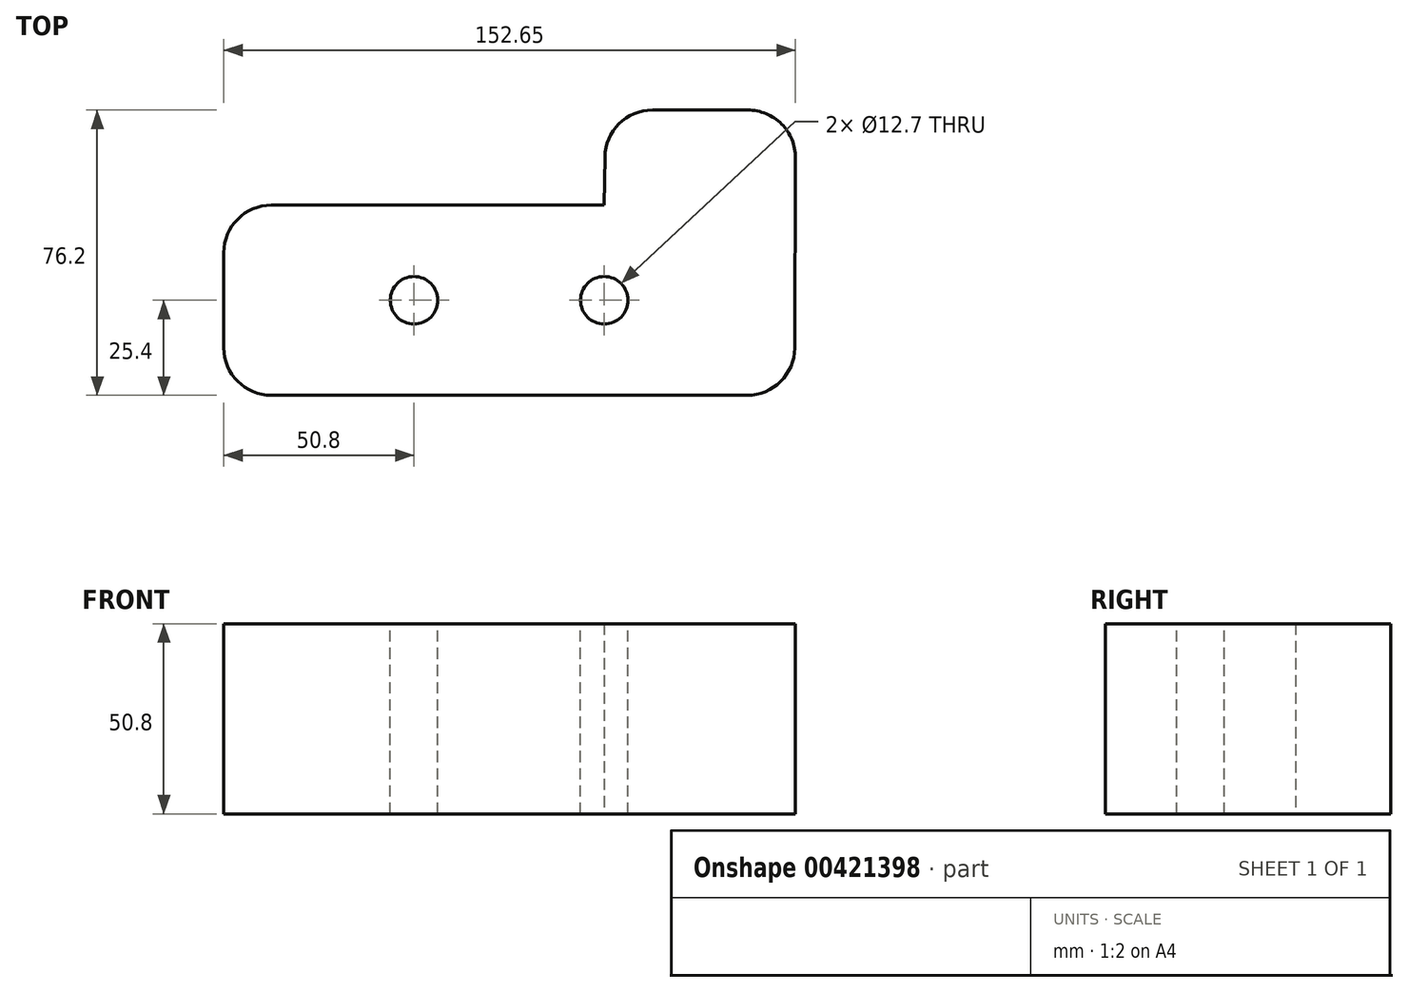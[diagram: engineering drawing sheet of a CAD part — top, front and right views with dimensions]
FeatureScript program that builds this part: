
annotation { "Feature Type Name" : "Feature", "Feature Type Description" : "" }
export const myFeature = defineFeature(function(context is Context, id is Id, definition is map)
    precondition{}
    {
        {
            var Q0;
            Q0=qCreatedBy(makeId("Top.planeOp"),FACE);
            var sketch = newSketch(context, id + "F0", { "sketchPlane" : qUnion([Q0])});
            skLineSegment(sketch, "E0", {"start": v(0, 0) * mm, "end": v(152.4, 0) * mm});
            skLineSegment(sketch, "E1", {"start": v(0, 0) * mm, "end": v(0, 50.8) * mm});
            skLineSegment(sketch, "E2", {"start": v(0, 50.8) * mm, "end": v(101.6, 50.8) * mm});
            skLineSegment(sketch, "E3", {"start": v(101.6, 50.8) * mm, "end": v(101.6, 76.2) * mm});
            skLineSegment(sketch, "E4", {"start": v(101.9, 76.2) * mm, "end": v(152.7, 76.2) * mm});
            skLineSegment(sketch, "E5", {"start": v(152.7, 76.2) * mm, "end": v(152.4, 0) * mm});
            skLineSegment(sketch, "E6", {"start": v(101.9, 76.2) * mm, "end": v(101.6, 50.8) * mm});
            skSolve(sketch);
        }
        {
            var Q0;
            Q0=makeQuery(id+"F0.imprint","IMPRINT",FACE,{"disambiguationData":[TD([[makeQuery(id+"F0.imprint","IMPRINT",EDGE,{"derivedFrom":sQuery(id+"F0.wireOp",EDGE,"E0")}),1.0]])]});
            extrude(context, id + "F1", {"entities" : qUnion([Q0]), "depth" : 50.8 * mm});
        }
        {
            var Q0;
            Q0=makeQuery(id+"F1.opExtrude","SWEPT_EDGE",EDGE,{"disambiguationData":[OSD([sQuery(id+"F0.wireOp",EDGE,"E5"),sQuery(id+"F0.wireOp",EDGE,"E4")])]});
            var Q1;
            Q1=makeQuery(id+"F1.opExtrude","SWEPT_EDGE",EDGE,{"disambiguationData":[OSD([sQuery(id+"F0.wireOp",EDGE,"E1"),sQuery(id+"F0.wireOp",EDGE,"E2")])]});
            var Q2;
            Q2=makeQuery(id+"F1.opExtrude","SWEPT_EDGE",EDGE,{"disambiguationData":[OSD([sQuery(id+"F0.wireOp",EDGE,"E0"),sQuery(id+"F0.wireOp",EDGE,"E1")])]});
            var Q3;
            Q3=makeQuery(id+"F1.opExtrude","SWEPT_EDGE",EDGE,{"disambiguationData":[OSD([sQuery(id+"F0.wireOp",EDGE,"E0"),sQuery(id+"F0.wireOp",EDGE,"E5")])]});
            fillet(context, id + "F2", {"entities" : qUnion([Q0, Q1, Q2, Q3]), "radius" : 12.7 * mm, "tangentPropagation" : true, "allowEdgeOverflow" : false});
        }
        {
            var Q0;
            Q0=makeQuery(id+"F1.opExtrude","CAP_FACE",FACE,{"disambiguationData":[OSD([sQuery(id+"F0.wireOp",EDGE,"E0"),sQuery(id+"F0.wireOp",EDGE,"E1"),sQuery(id+"F0.wireOp",EDGE,"E2"),sQuery(id+"F0.wireOp",EDGE,"E5"),sQuery(id+"F0.wireOp",EDGE,"E4"),sQuery(id+"F0.wireOp",EDGE,"E6")])],"isStart":false});
            var sketch = newSketch(context, id + "F3", { "sketchPlane" : qUnion([Q0])});
            skPoint(sketch, "E7", {"position": v(50.8, 25.4) * mm});
            skPoint(sketch, "E7.positionSnap0", {"position": v(0, 25.4) * mm});
            skPoint(sketch, "E8", {"position": v(101.6, 25.4) * mm});
            skSolve(sketch);
        }
        {
            var Q0;
            Q0=sQuery(id+"F3.wireOp",VERTEX,"E7");
            var Q1;
            Q1=sQuery(id+"F3.wireOp",VERTEX,"E8");
            var Q2;
            Q2=makeQuery(id+"F1.opExtrude","SWEPT_BODY",BODY,{"disambiguationData":[OSD([sQuery(id+"F0.wireOp",EDGE,"E0"),sQuery(id+"F0.wireOp",EDGE,"E1"),sQuery(id+"F0.wireOp",EDGE,"E2"),sQuery(id+"F0.wireOp",EDGE,"E5"),sQuery(id+"F0.wireOp",EDGE,"E4"),sQuery(id+"F0.wireOp",EDGE,"E6")])]});
            hole(context, id + "F4", {"style" : HoleStyle.SIMPLE, "endStyle" : HoleEndStyle.THROUGH, "holeDiameter" : 12.7 * mm, "isTappedThrough" : true, "tappedDepth" : 12.7 * mm, "tapClearance" : 3, "locations" : qUnion([Q0, Q1]), "scope" : qUnion([Q2])});
        }
    });
